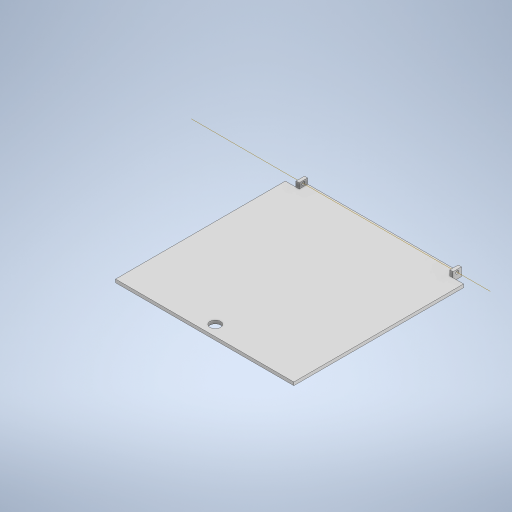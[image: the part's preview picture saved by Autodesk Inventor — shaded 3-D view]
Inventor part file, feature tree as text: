
AUTODESK INVENTOR PART (.ipt)
format: ipt  version: 2024.3 (Build 283343000, 343)  size: 274,432 bytes
history: native  units: mm
features: sketch x5, extrude x3, other x2, mirror x2, hole x2
ambient origin geometry x8: Origin, YZ Plane, XZ Plane, XY Plane, X Axis, Y Axis, Z Axis, Center Point
bodies: Body1 (feature_tree)
feature tree (14):
  other  "Těleso1"
  extrude  "Vysunutí1"  Depth=168.0mm
  sketch  "Náčrt2"
  extrude  "Vysunutí3"  Depth=168.0mm
  mirror  "Zrcadlit1"
  hole  "Díra1"  [1 undecoded]
  extrude  "Vysunutí4"  Depth=10.0mm
  hole  "Díra2"  [1 undecoded]
  mirror  "Zrcadlit2"
  other  "Pracovní osa1"
  sketch  "Náčrt1"
  sketch  "Náčrt3"
  sketch  "Náčrt4"
  sketch  "Náčrt5"
note: 2 required parameter values undecoded (feature->parameter linkage not recoverable at this tier; creation-order binding heuristic only, values carry confidence <= 0.55)
